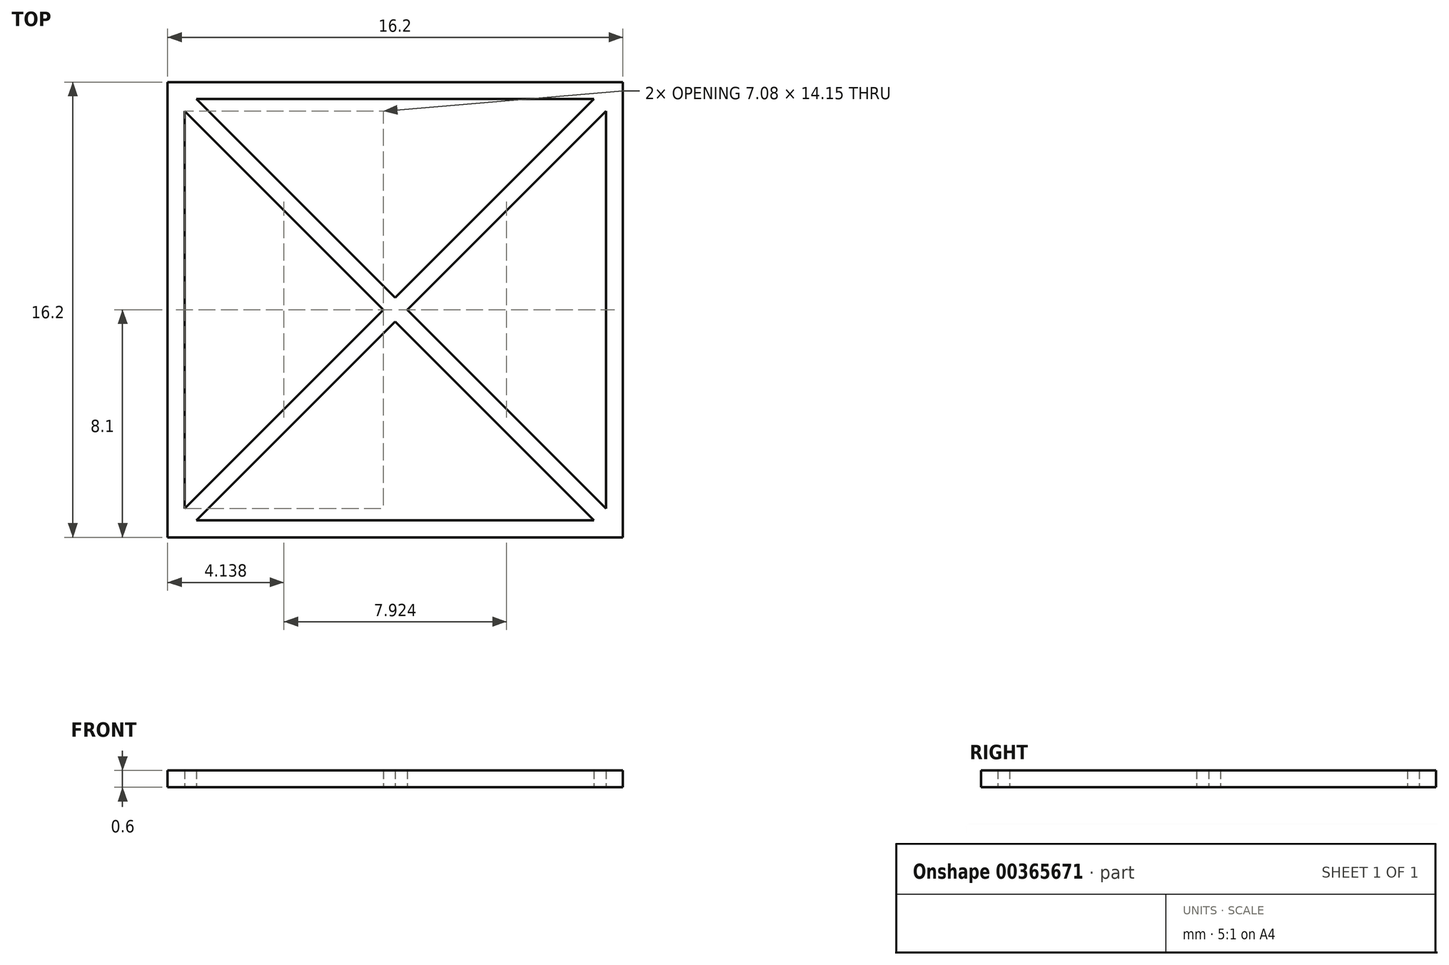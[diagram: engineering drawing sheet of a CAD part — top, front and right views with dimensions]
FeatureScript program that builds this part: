
annotation { "Feature Type Name" : "Feature", "Feature Type Description" : "" }
export const myFeature = defineFeature(function(context is Context, id is Id, definition is map)
    precondition{}
    {
        {
            var Q0;
            Q0=qCreatedBy(makeId("Top.planeOp"),FACE);
            var sketch = newSketch(context, id + "F0", { "sketchPlane" : qUnion([Q0])});
            skPoint(sketch, "E0", {"position": v(0, 0) * mm});
            skPoint(sketch, "E1", {"position": v(7.5, 0) * mm});
            skPoint(sketch, "E2", {"position": v(0, 7.5) * mm});
            skPoint(sketch, "E3", {"position": v(-7.5, 0) * mm});
            skPoint(sketch, "E4", {"position": v(0, -7.5) * mm});
            skPoint(sketch, "E5", {"position": v(-7.5, 7.5) * mm});
            skLineSegment(sketch, "E6.bottom", {"start": v(-7.5, 7.5) * mm, "end": v(7.5, 7.5) * mm});
            skLineSegment(sketch, "E6.top", {"start": v(-7.5, -7.5) * mm, "end": v(7.5, -7.5) * mm});
            skLineSegment(sketch, "E6.left", {"start": v(-7.5, 7.5) * mm, "end": v(-7.5, -7.5) * mm});
            skLineSegment(sketch, "E6.right", {"start": v(7.5, 7.5) * mm, "end": v(7.5, -7.5) * mm});
            skPoint(sketch, "E7", {"position": v(0, 8.1) * mm});
            skPoint(sketch, "E8", {"position": v(8.1, 0) * mm});
            skPoint(sketch, "E9", {"position": v(0, -8.1) * mm});
            skPoint(sketch, "E10", {"position": v(-8.1, 0) * mm});
            skLineSegment(sketch, "E11", {"start": v(0, 8.1) * mm, "end": v(8.1, 8.1) * mm});
            skLineSegment(sketch, "E12", {"start": v(8.1, 8.1) * mm, "end": v(8.1, -8.1) * mm});
            skLineSegment(sketch, "E13", {"start": v(8.1, -8.1) * mm, "end": v(0, -8.1) * mm});
            skLineSegment(sketch, "E14", {"start": v(0, 11.68) * mm, "end": v(0, -10.66) * mm});
            skLineSegment(sketch, "E15.MirrorCS", {"start": v(0, 8.1) * mm, "end": v(-8.1, 8.1) * mm});
            skLineSegment(sketch, "E16.MirrorCS", {"start": v(-8.1, 8.1) * mm, "end": v(-8.1, -8.1) * mm});
            skLineSegment(sketch, "E17.MirrorCS", {"start": v(-8.1, -8.1) * mm, "end": v(0, -8.1) * mm});
            skLineSegment(sketch, "E18", {"start": v(-7.5, 7.5) * mm, "end": v(7.5, -7.5) * mm});
            skLineSegment(sketch, "E19", {"start": v(7.5, 7.5) * mm, "end": v(-7.5, -7.5) * mm});
            skLineSegment(sketch, "E20", {"start": v(-7.08, 7.5) * mm, "end": v(7.5, -7.08) * mm});
            skLineSegment(sketch, "E21", {"start": v(-7.5, 7.08) * mm, "end": v(7.08, -7.5) * mm});
            skLineSegment(sketch, "E22", {"start": v(-7.08, -7.5) * mm, "end": v(7.5, 7.08) * mm});
            skLineSegment(sketch, "E23", {"start": v(7.08, 7.5) * mm, "end": v(-7.5, -7.08) * mm});
            skSolve(sketch);
        }
        {
            var Q0;
            {var subQ0=sQuery(id+"F0.wireOp",EDGE,"E19");var subQ3=sQuery(id+"F0.wireOp",EDGE,"E21");var subQ5=makeQuery(id+"F0.imprint","INTERSECT",VERTEX,{"derivedFrom":[subQ0,subQ3]});Q0=makeQuery(id+"F0.imprint","IMPRINT",FACE,{"disambiguationData":[TD([[makeQuery(id+"F0.imprint","IMPRINT",EDGE,{"disambiguationData":[TD([[subQ5,1.0]])],"derivedFrom":subQ0}),1.0]])]});}
            var Q1;
            {var subQ1=sQuery(id+"F0.wireOp",EDGE,"E6.bottom");var subQ3=sQuery(id+"F0.wireOp",EDGE,"E20");var subQ4=makeQuery(id+"F0.imprint","INTERSECT",VERTEX,{"derivedFrom":[subQ1,subQ3]});Q1=makeQuery(id+"F0.imprint","IMPRINT",FACE,{"disambiguationData":[TD([[makeQuery(id+"F0.imprint","IMPRINT",EDGE,{"disambiguationData":[TD([[subQ4,1.0]])],"derivedFrom":subQ1}),-1.0]])]});}
            var Q2;
            {var subQ0=sQuery(id+"F0.wireOp",EDGE,"E19");var subQ5=sQuery(id+"F0.wireOp",EDGE,"E21");var subQ6=makeQuery(id+"F0.imprint","INTERSECT",VERTEX,{"derivedFrom":[subQ0,subQ5]});Q2=makeQuery(id+"F0.imprint","IMPRINT",FACE,{"disambiguationData":[TD([[makeQuery(id+"F0.imprint","IMPRINT",EDGE,{"disambiguationData":[TD([[subQ6,1.0]])],"derivedFrom":subQ5}),-1.0]])]});}
            var Q3;
            {var subQ0=sQuery(id+"F0.wireOp",EDGE,"E19");var subQ5=sQuery(id+"F0.wireOp",EDGE,"E20");var subQ6=makeQuery(id+"F0.imprint","INTERSECT",VERTEX,{"derivedFrom":[subQ0,subQ5]});Q3=makeQuery(id+"F0.imprint","IMPRINT",FACE,{"disambiguationData":[TD([[makeQuery(id+"F0.imprint","IMPRINT",EDGE,{"disambiguationData":[TD([[subQ6,-1.0]])],"derivedFrom":subQ5}),1.0]])]});}
            var Q4;
            {var subQ0=sQuery(id+"F0.wireOp",EDGE,"E15.MirrorCS");Q4=makeQuery(id+"F0.imprint","IMPRINT",FACE,{"disambiguationData":[TD([[makeQuery(id+"F0.imprint","IMPRINT",EDGE,{"derivedFrom":subQ0}),1.0]])]});}
            var Q5;
            {var subQ3=sQuery(id+"F0.wireOp",EDGE,"E19");var subQ5=sQuery(id+"F0.wireOp",EDGE,"E20");var subQ6=makeQuery(id+"F0.imprint","INTERSECT",VERTEX,{"derivedFrom":[subQ3,subQ5]});Q5=makeQuery(id+"F0.imprint","IMPRINT",FACE,{"disambiguationData":[TD([[makeQuery(id+"F0.imprint","IMPRINT",EDGE,{"disambiguationData":[TD([[subQ6,-1.0]])],"derivedFrom":subQ5}),-1.0]])]});}
            var Q6;
            {var subQ0=sQuery(id+"F0.wireOp",EDGE,"E23");var subQ3=sQuery(id+"F0.wireOp",EDGE,"E18");var subQ5=makeQuery(id+"F0.imprint","INTERSECT",VERTEX,{"derivedFrom":[subQ3,subQ0]});Q6=makeQuery(id+"F0.imprint","IMPRINT",FACE,{"disambiguationData":[TD([[makeQuery(id+"F0.imprint","IMPRINT",EDGE,{"disambiguationData":[TD([[subQ5,-1.0]])],"derivedFrom":subQ3}),1.0]])]});}
            var Q7;
            {var subQ1=sQuery(id+"F0.wireOp",EDGE,"E6.top");var subQ3=sQuery(id+"F0.wireOp",EDGE,"E22");var subQ4=makeQuery(id+"F0.imprint","INTERSECT",VERTEX,{"derivedFrom":[subQ1,subQ3]});Q7=makeQuery(id+"F0.imprint","IMPRINT",FACE,{"disambiguationData":[TD([[makeQuery(id+"F0.imprint","IMPRINT",EDGE,{"disambiguationData":[TD([[subQ4,1.0]])],"derivedFrom":subQ1}),1.0]])]});}
            var Q8;
            {var subQ1=sQuery(id+"F0.wireOp",EDGE,"E6.top");var subQ3=sQuery(id+"F0.wireOp",EDGE,"E21");var subQ4=makeQuery(id+"F0.imprint","INTERSECT",VERTEX,{"derivedFrom":[subQ1,subQ3]});Q8=makeQuery(id+"F0.imprint","IMPRINT",FACE,{"disambiguationData":[TD([[makeQuery(id+"F0.imprint","IMPRINT",EDGE,{"disambiguationData":[TD([[subQ4,-1.0]])],"derivedFrom":subQ1}),1.0]])]});}
            var Q9;
            {var subQ3=sQuery(id+"F0.wireOp",EDGE,"E19");var subQ5=sQuery(id+"F0.wireOp",EDGE,"E21");var subQ6=makeQuery(id+"F0.imprint","INTERSECT",VERTEX,{"derivedFrom":[subQ3,subQ5]});Q9=makeQuery(id+"F0.imprint","IMPRINT",FACE,{"disambiguationData":[TD([[makeQuery(id+"F0.imprint","IMPRINT",EDGE,{"disambiguationData":[TD([[subQ6,1.0]])],"derivedFrom":subQ5}),1.0]])]});}
            var Q10;
            {var subQ12=sQuery(id+"F0.wireOp",EDGE,"E11");Q10=makeQuery(id+"F0.imprint","IMPRINT",FACE,{"disambiguationData":[TD([[makeQuery(id+"F0.imprint","IMPRINT",EDGE,{"derivedFrom":subQ12}),-1.0]])]});}
            var Q11;
            {var subQ1=sQuery(id+"F0.wireOp",EDGE,"E6.right");var subQ3=sQuery(id+"F0.wireOp",EDGE,"E20");var subQ4=makeQuery(id+"F0.imprint","INTERSECT",VERTEX,{"derivedFrom":[subQ1,subQ3]});Q11=makeQuery(id+"F0.imprint","IMPRINT",FACE,{"disambiguationData":[TD([[makeQuery(id+"F0.imprint","IMPRINT",EDGE,{"disambiguationData":[TD([[subQ4,1.0]])],"derivedFrom":subQ3}),-1.0]])]});}
            var Q12;
            {var subQ1=sQuery(id+"F0.wireOp",EDGE,"E6.bottom");var subQ3=sQuery(id+"F0.wireOp",EDGE,"E23");var subQ4=makeQuery(id+"F0.imprint","INTERSECT",VERTEX,{"derivedFrom":[subQ1,subQ3]});Q12=makeQuery(id+"F0.imprint","IMPRINT",FACE,{"disambiguationData":[TD([[makeQuery(id+"F0.imprint","IMPRINT",EDGE,{"disambiguationData":[TD([[subQ4,-1.0]])],"derivedFrom":subQ1}),-1.0]])]});}
            var Q13;
            {var subQ0=sQuery(id+"F0.wireOp",EDGE,"E18");var subQ3=sQuery(id+"F0.wireOp",EDGE,"E22");var subQ5=makeQuery(id+"F0.imprint","INTERSECT",VERTEX,{"derivedFrom":[subQ0,subQ3]});Q13=makeQuery(id+"F0.imprint","IMPRINT",FACE,{"disambiguationData":[TD([[makeQuery(id+"F0.imprint","IMPRINT",EDGE,{"disambiguationData":[TD([[subQ5,1.0]])],"derivedFrom":subQ0}),-1.0]])]});}
            var Q14;
            {var subQ0=sQuery(id+"F0.wireOp",EDGE,"E20");var subQ3=sQuery(id+"F0.wireOp",EDGE,"E19");var subQ5=makeQuery(id+"F0.imprint","INTERSECT",VERTEX,{"derivedFrom":[subQ3,subQ0]});Q14=makeQuery(id+"F0.imprint","IMPRINT",FACE,{"disambiguationData":[TD([[makeQuery(id+"F0.imprint","IMPRINT",EDGE,{"disambiguationData":[TD([[subQ5,-1.0]])],"derivedFrom":subQ3}),-1.0]])]});}
            var Q15;
            {var subQ1=sQuery(id+"F0.wireOp",EDGE,"E6.left");var subQ3=sQuery(id+"F0.wireOp",EDGE,"E21");var subQ4=makeQuery(id+"F0.imprint","INTERSECT",VERTEX,{"derivedFrom":[subQ1,subQ3]});Q15=makeQuery(id+"F0.imprint","IMPRINT",FACE,{"disambiguationData":[TD([[makeQuery(id+"F0.imprint","IMPRINT",EDGE,{"disambiguationData":[TD([[subQ4,-1.0]])],"derivedFrom":subQ3}),1.0]])]});}
            extrude(context, id + "F1", {"entities" : qUnion([Q0, Q1, Q2, Q3, Q4, Q5, Q6, Q7, Q8, Q9, Q10, Q11, Q12, Q13, Q14, Q15]), "depth" : 0.6 * mm});
        }
    });
